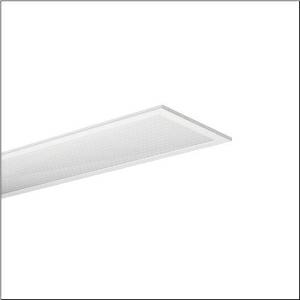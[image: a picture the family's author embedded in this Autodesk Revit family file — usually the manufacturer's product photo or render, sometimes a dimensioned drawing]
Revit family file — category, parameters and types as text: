
# Revit family: apollon_r__21_linear_51mq14wd2t12_0b39
name_source: partatom
category: Lighting Fixtures
units: mm (PartAtom-declared; Revit-internal decimal feet)

## family parameters
Cut with Voids When Loaded = No
Host = Face
Light Source = No
Part Type = Normal
Room Calculation Point = No
Round Connector Dimension = Use Diameter
Shared = No

## types (1)
- --- (1 x LED 2700 K ... 6500 K, 4200 lm, 44 W, 6500K)
    Apparent Load = 44 VA
    CIE Flux Codes = 60 87 97 100 100
    Color Rendering = 80
    Color Temperature = 6500K
    Default Elevation = 1800 mm
    Description = Apollon® 21 linear, office luminaire, primary optical cover: micro prismatic cover, of PMMA, CAT 2 (L<= 3000cd/m²), light emission: direct distribution, primary light characteristic: symmetric, installation type: lay-in mounting, LED, rated luminous flux: 4.200lm, luminous efficacy: 96lm/W, light colour: 8tw, colour temperature: 2700..6500K, control gear: DALI DT8, with terminal, 5-pole, mains connection: 220..240V, AC, 50/60Hz, rated input power: 44W, housing, of aluminium, coated, pure white, length: 1.245mm, width: 307mm, height: 30mm, housing upper side, of sheet steel, galvanised, protection rating (complete): IP20, protection rating (lamp compartment, on room side): IP50, insulation class (complete): insulation class I (protective earthing), certification: CE, ENEC, packaging unit: 1 piece
    Height = 0 mm  [stored 0 ft]
    Lamp = 1 x LED 2700 K ... 6500 K
    Lamp Light Flux = 4200 lm
    Lamp Power = 44 W
    Lamp count = 1
    Length = 1245 mm
    Luminous efficacy = 95 lm/W
    Manufacturer = Siteco
    ModVariant = No
    Model = 51MQ14WD2T12
    Mounting Place = Ceiling
    Mounting Type = Recessed
    Number of Poles = 1
    OnlyDefault = Yes
    Power Factor = 1
    Product Name = Apollon® 21 linear
    Product group = office luminaire | ceiling recessed
    ProductGroupID = 401
    Protection Class = Protection class I
    Protection Degree = IP 20
    RLX_Detail_Level = 1
    RLX_Emergency_Light_Flux = 0 lm
    RLX_Emergency_Type = 0
    RLX_Emergency_Type_DB = No
    RlxData = <blob elided: 17589 chars, md5=fae814d7>
    Socket = socket
    Standby Power = 0 W
    System Light Flux = 4200 lm
    System Power = 44 W
    Type Comments = individual setting: CCT=6500K, colour temperature 6500K
    Type Image = l_1291045.jpg
    URL = http://relux.com
    VarID = @adj_197682
    Voltage = 0 V
    Weight = 0.00 kg
    Width = 307 mm

note: [stored X ft] marks values corroborated as IEEE doubles in the binary element streams (Revit-internal decimal feet)

## geometry (parser evidence)
native form markers: Blend x4, Sweep x10
no freeform markers — native parametric forms only
